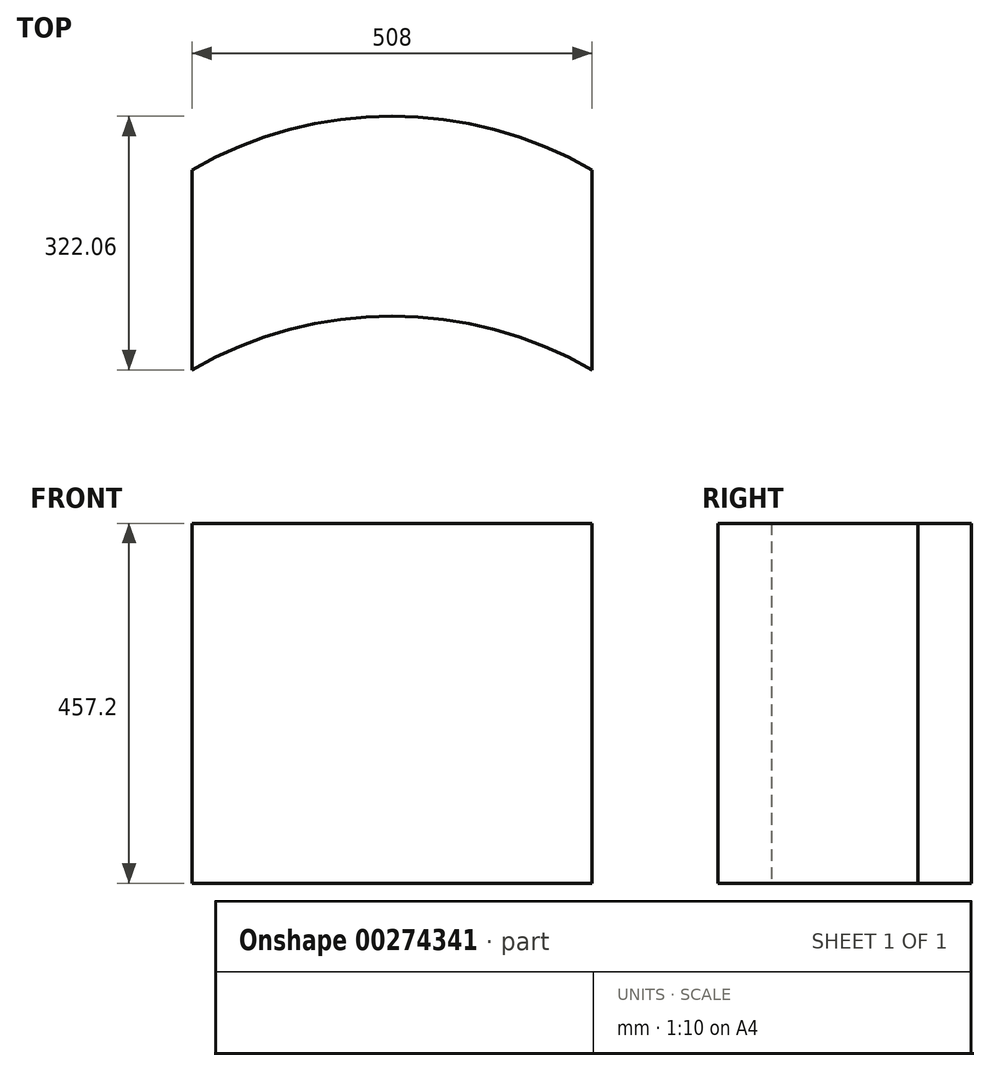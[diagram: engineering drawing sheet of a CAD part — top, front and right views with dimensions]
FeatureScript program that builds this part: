
annotation { "Feature Type Name" : "Feature", "Feature Type Description" : "" }
export const myFeature = defineFeature(function(context is Context, id is Id, definition is map)
    precondition{}
    {
        {
            var Q0;
            Q0=qCreatedBy(makeId("Top.planeOp"),FACE);
            var sketch = newSketch(context, id + "F0", { "sketchPlane" : qUnion([Q0])});
            skLineSegment(sketch, "E0", {"start": v(-751.56, 0) * mm, "end": v(-751.56, -254) * mm});
            skLineSegment(sketch, "E1", {"start": v(-751.56, -254) * mm, "end": v(-243.56, -254) * mm});
            skArc(sketch, "E2", {"start": v(-243.56, -254) * mm, "mid": v(-497.56, -185.94) * mm, "end": v(-751.56, -254) * mm});
            skLineSegment(sketch, "E3", {"start": v(-243.56, -254) * mm, "end": v(-243.56, 0) * mm});
            skArc(sketch, "E4", {"start": v(-243.56, 0) * mm, "mid": v(-497.56, 68.06) * mm, "end": v(-751.56, 0) * mm});
            skSolve(sketch);
        }
        {
            var Q0;
            Q0=makeQuery(id+"F0.imprint","IMPRINT",FACE,{"disambiguationData":[TD([[makeQuery(id+"F0.imprint","IMPRINT",EDGE,{"derivedFrom":sQuery(id+"F0.wireOp",EDGE,"E0")}),1.0]])]});
            extrude(context, id + "F1", {"entities" : qUnion([Q0]), "depth" : 457.2 * mm});
        }
    });
